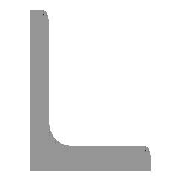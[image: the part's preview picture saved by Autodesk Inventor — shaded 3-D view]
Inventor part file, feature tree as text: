
AUTODESK INVENTOR PART (.ipt)
format: ipt  version: 2022.1 (Build 261234000, 234)  size: 135,680 bytes
history: native  units: mm (DEFAULTED — no unit token found)
features: other x4, sketch x3, plane x1
ambient origin geometry x8: Origin, YZ Plane, XZ Plane, XY Plane, X Axis, Y Axis, Z Axis, Center Point
bodies: Solid1 (feature_tree), Body (feature_tree)
feature tree (8):
  parser-record x1  (decoder bookkeeping rows leaked as tree rows — omitted from the tree; the rows remain in map.json)
  other  "Driven Length"
  other  "Start Plane"
  other  "End Plane"
  sketch  "Sketch"  dims[d5=50.0mm d6=30.0mm d7=4.0mm d8=3.0mm d9=4.0mm d10=3.0mm d11=1680.0mm d12=0.0mm d17=5.0mm d18=2.5mm d19=8.3mm d20=8.3mm d21=-0.0mm d22=1680.0mm d23=90.0deg d24=1680.0mm]
  sketch  "Sketch3"  dims[d3=50.0mm]
  plane  "Work Plane10"
  sketch  "Sketch4"  dims[d4=30.0mm]
